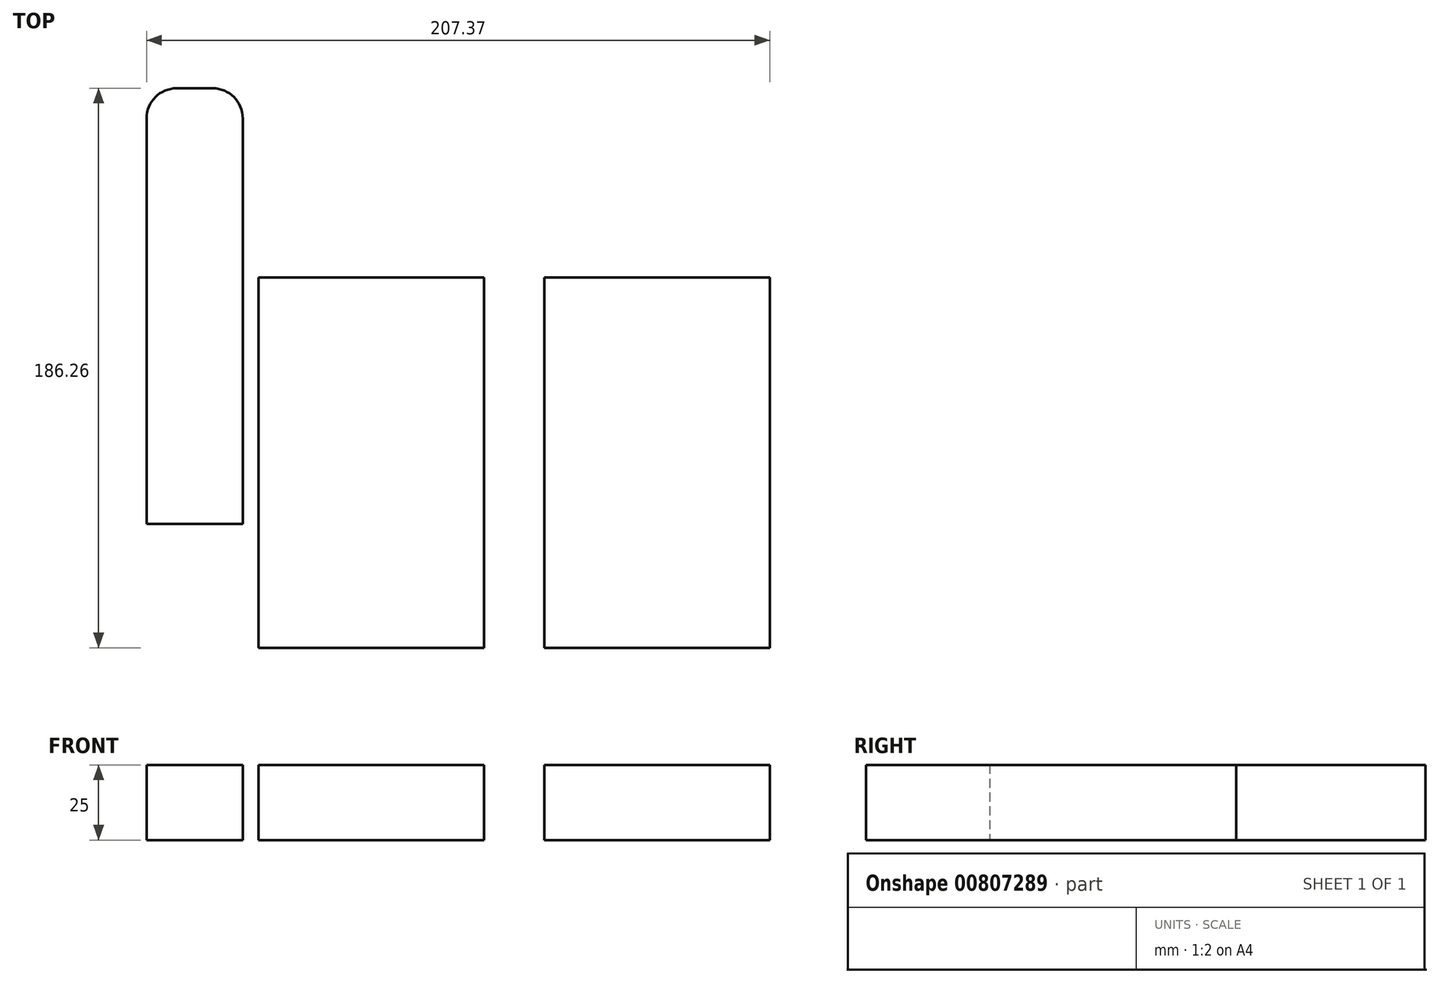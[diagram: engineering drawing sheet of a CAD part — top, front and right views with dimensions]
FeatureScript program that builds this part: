
annotation { "Feature Type Name" : "Feature", "Feature Type Description" : "" }
export const myFeature = defineFeature(function(context is Context, id is Id, definition is map)
    precondition{}
    {
        {
            var Q0;
            Q0=qCreatedBy(makeId("Top.planeOp"),FACE);
            var sketch = newSketch(context, id + "F0", { "sketchPlane" : qUnion([Q0])});
            skLineSegment(sketch, "E0.bottom", {"start": v(-167.72, 88.11) * mm, "end": v(-155.72, 88.11) * mm});
            skLineSegment(sketch, "E0.top", {"start": v(-177.72, -56.89) * mm, "end": v(-145.72, -56.89) * mm});
            skLineSegment(sketch, "E0.left", {"start": v(-177.72, 78.11) * mm, "end": v(-177.72, -56.89) * mm});
            skLineSegment(sketch, "E0.right", {"start": v(-145.72, 78.11) * mm, "end": v(-145.72, -56.89) * mm});
            skLineSegment(sketch, "E1.bottom", {"start": v(-140.44, 25.15) * mm, "end": v(-65.43, 25.15) * mm});
            skLineSegment(sketch, "E1.top", {"start": v(-140.44, -98.15) * mm, "end": v(-65.43, -98.15) * mm});
            skLineSegment(sketch, "E1.left", {"start": v(-140.44, 25.15) * mm, "end": v(-140.44, -98.15) * mm});
            skLineSegment(sketch, "E1.right", {"start": v(-65.43, 25.15) * mm, "end": v(-65.43, -98.15) * mm});
            skLineSegment(sketch, "E2.bottom", {"start": v(-45.35, 25.15) * mm, "end": v(29.65, 25.15) * mm});
            skLineSegment(sketch, "E2.top", {"start": v(-45.35, -98.15) * mm, "end": v(29.65, -98.15) * mm});
            skLineSegment(sketch, "E2.left", {"start": v(-45.35, 25.15) * mm, "end": v(-45.35, -98.15) * mm});
            skLineSegment(sketch, "E2.right", {"start": v(29.65, 25.15) * mm, "end": v(29.65, -98.15) * mm});
            skPoint(sketch, "E3.visualSharp", {"position": v(-177.72, 88.11) * mm});
            skArc(sketch, "E3.filletArc", {"start": v(-167.72, 88.11) * mm, "mid": v(-174.8, 85.18) * mm, "end": v(-177.72, 78.11) * mm});
            skPoint(sketch, "E4.visualSharp", {"position": v(-145.72, 88.11) * mm});
            skArc(sketch, "E4.filletArc", {"start": v(-145.72, 78.11) * mm, "mid": v(-148.65, 85.18) * mm, "end": v(-155.72, 88.11) * mm});
            skSolve(sketch);
        }
        {
            var Q0;
            Q0=makeQuery(id+"F0.imprint","IMPRINT",FACE,{"disambiguationData":[TD([[makeQuery(id+"F0.imprint","IMPRINT",EDGE,{"derivedFrom":sQuery(id+"F0.wireOp",EDGE,"E0.bottom")}),-1.0]])]});
            var Q1;
            Q1=makeQuery(id+"F0.imprint","IMPRINT",FACE,{"disambiguationData":[TD([[makeQuery(id+"F0.imprint","IMPRINT",EDGE,{"derivedFrom":sQuery(id+"F0.wireOp",EDGE,"E1.bottom")}),-1.0]])]});
            var Q2;
            Q2=makeQuery(id+"F0.imprint","IMPRINT",FACE,{"disambiguationData":[TD([[makeQuery(id+"F0.imprint","IMPRINT",EDGE,{"derivedFrom":sQuery(id+"F0.wireOp",EDGE,"E2.bottom")}),-1.0]])]});
            extrude(context, id + "F1", {"entities" : qUnion([Q0, Q1, Q2]), "depth" : 25 * mm, "offsetDistance" : 25 * mm});
        }
    });
